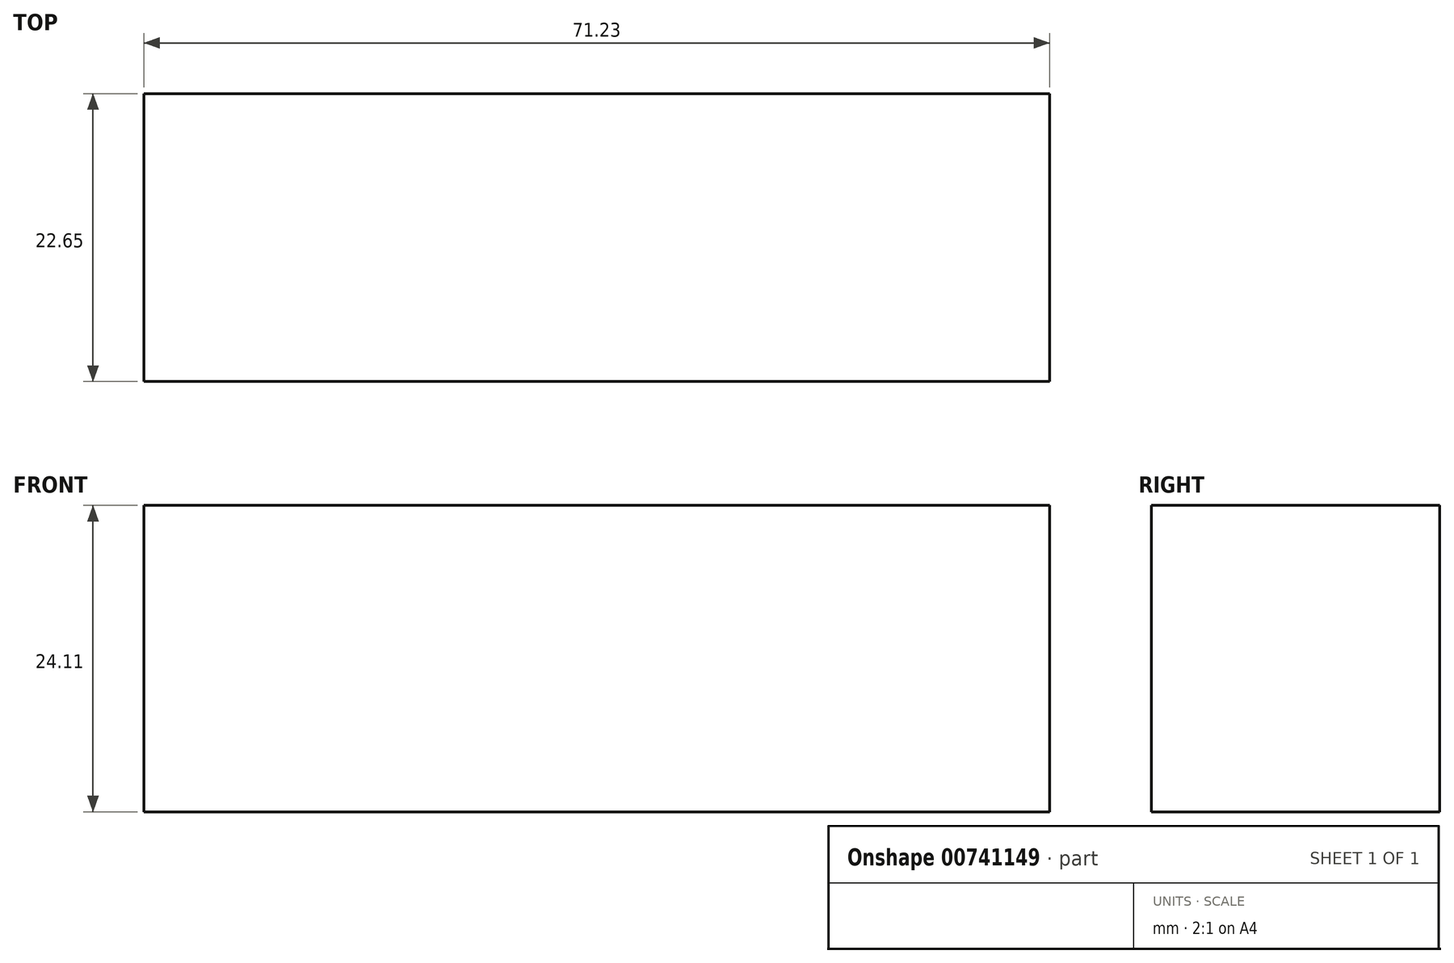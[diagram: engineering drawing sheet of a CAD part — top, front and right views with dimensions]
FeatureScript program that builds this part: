
annotation { "Feature Type Name" : "Feature", "Feature Type Description" : "" }
export const myFeature = defineFeature(function(context is Context, id is Id, definition is map)
    precondition{}
    {
        {
            var Q0;
            Q0=qCreatedBy(makeId("Front.planeOp"),FACE);
            var sketch = newSketch(context, id + "F0", { "sketchPlane" : qUnion([Q0])});
            skLineSegment(sketch, "E0.bottom", {"start": v(22.96, 45.29) * mm, "end": v(-48.27, 45.29) * mm});
            skLineSegment(sketch, "E0.top", {"start": v(22.96, 21.18) * mm, "end": v(-48.27, 21.18) * mm});
            skLineSegment(sketch, "E0.left", {"start": v(22.96, 45.29) * mm, "end": v(22.96, 21.18) * mm});
            skLineSegment(sketch, "E0.right", {"start": v(-48.27, 45.29) * mm, "end": v(-48.27, 21.18) * mm});
            skSolve(sketch);
        }
        {
            var Q0;
            Q0=makeQuery(id+"F0.imprint","IMPRINT",FACE,{"disambiguationData":[TD([[makeQuery(id+"F0.imprint","IMPRINT",EDGE,{"derivedFrom":sQuery(id+"F0.wireOp",EDGE,"E0.bottom")}),1.0]])]});
            extrude(context, id + "F1", {"entities" : qUnion([Q0]), "depth" : 22.65 * mm, "offsetDistance" : 25.4 * mm});
        }
    });
